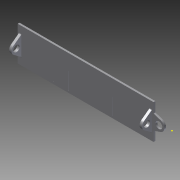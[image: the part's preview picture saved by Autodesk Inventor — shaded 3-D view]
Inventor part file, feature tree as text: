
AUTODESK INVENTOR PART (.ipt)
format: ipt  version: 2012 SP2 (Build 160219200, 219)  size: 223,232 bytes
history: native  units: in
note: dims shown in document units (in); Inventor stores cm internally (conversion verified against a paired STEP export)
features: sketch x7, extrude x6, pattern_linear x2, fillet x1, projected_geometry x1
ambient origin geometry x8: Origin, YZ Plane, XZ Plane, XY Plane, X Axis, Y Axis, Z Axis, Center Point
bodies: Solid1 (feature_tree)
feature tree (17):
  sketch  "Sketch1"  dims[d0=11.0236in d1=2.7559in]
  extrude  "Extrusion1"  Depth=2.7559in
  extrude  "Extrusion2"  Depth=0.1437in TaperAngle=0.0deg
  extrude  "Extrusion3"  Depth=1.9685in
  pattern_linear  "Rectangular Pattern1"  Count1=2  [1 undecoded]
  extrude  "Extrusion4"  Depth=0.7874in
  pattern_linear  "Rectangular Pattern2"  Count1=6 Spacing1=0.3937in
  extrude  "Extrusion5"  Depth=2.3622in
  extrude  "Extrusion6"  Depth=0.6973in TaperAngle=0.0deg
  fillet  "Fillet1"  Radius=0.0787in
  sketch  "Sketch2"  dims[d2=1.1811in d3=0.1437in d4=0.0in]
  sketch  "Sketch3"  dims[d5=0.1969in d6=1.9685in]
  sketch  "Sketch4"  dims[d7=1.3937in d8=0.0in d9=0.7874in]
  sketch  "Sketch5"  dims[d10=0.3937in d11=0.0in d12=0.7874in d14=10.4331in d15=2.3622in d17=1.1811in d18=0.3937in d20=0.3937in]
  sketch  "Sketch6"  dims[d22=0.0098in d23=0.0in d24=2.3622in d26=1.1811in]
  sketch  "Sketch7"  dims[d27=0.6973in d28=0.0in d29=0.6973in d30=0.0in d31=0.0787in]
  projected_geometry  "Projected Loop1"
note: 1 required parameter value undecoded (feature->parameter linkage not recoverable at this tier; creation-order binding heuristic only, values carry confidence <= 0.55)
